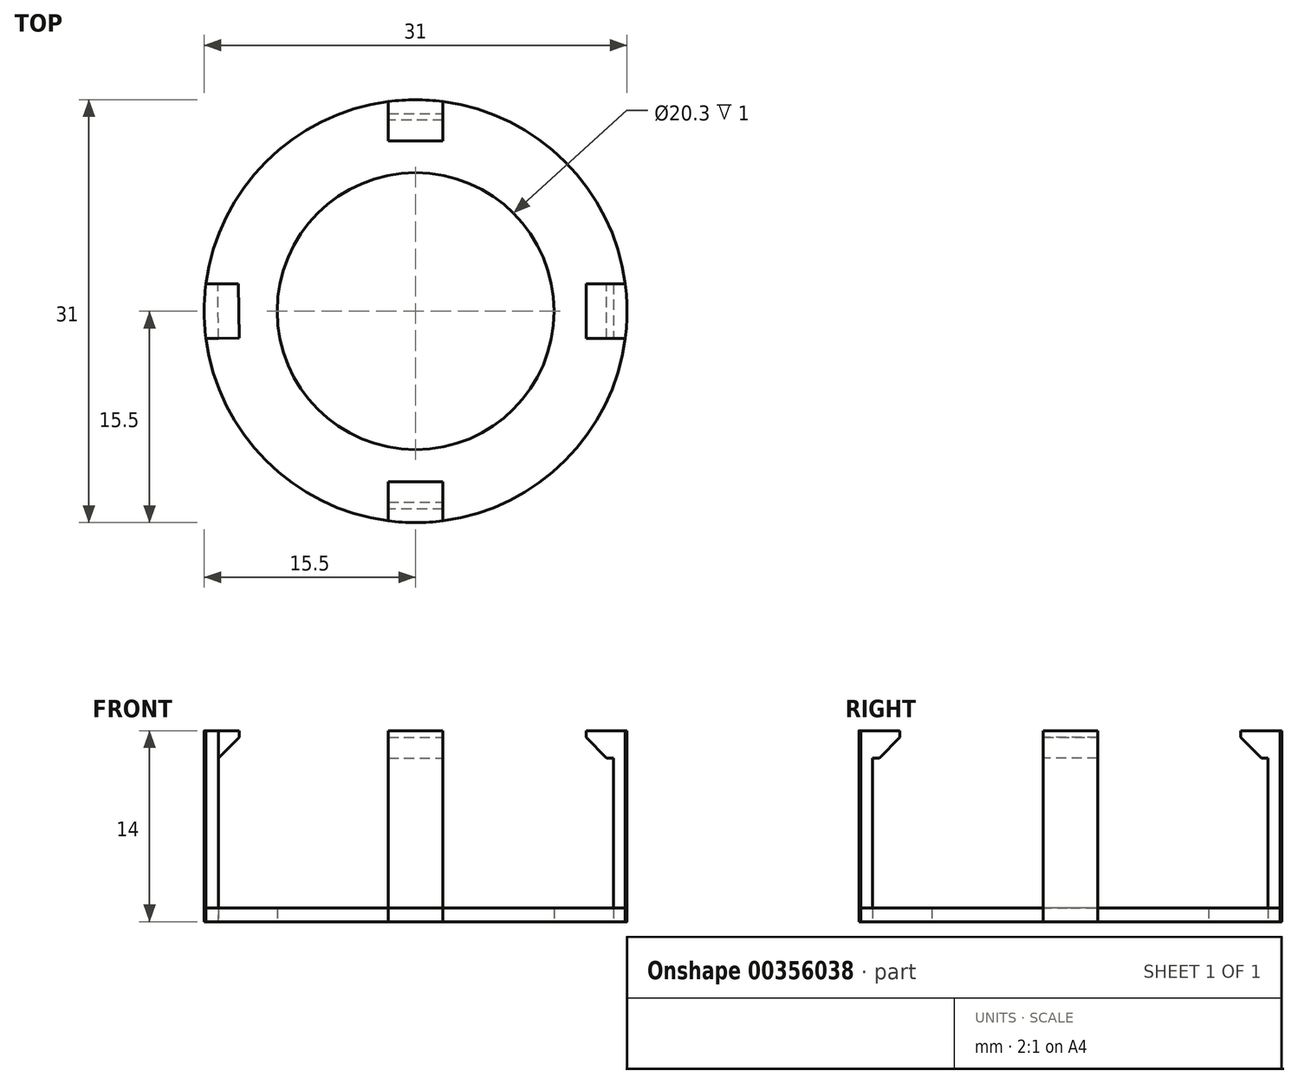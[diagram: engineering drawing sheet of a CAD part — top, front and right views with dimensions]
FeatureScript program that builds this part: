
annotation { "Feature Type Name" : "Feature", "Feature Type Description" : "" }
export const myFeature = defineFeature(function(context is Context, id is Id, definition is map)
    precondition{}
    {
        {
            var Q0;
            Q0=qCreatedBy(makeId("Top.planeOp"),FACE);
            var sketch = newSketch(context, id + "F0", { "sketchPlane" : qUnion([Q0])});
            skCircle(sketch, "E0", {"center": v(0, 0) * mm, "radius": 15.5 * mm});
            skCircle(sketch, "E1", {"center": v(0, 0) * mm, "radius": 10.15 * mm});
            skLineSegment(sketch, "E2.top", {"start": v(-2, 14.5) * mm, "end": v(2, 14.5) * mm});
            skLineSegment(sketch, "E2.left", {"start": v(-2, 15.37) * mm, "end": v(-2, 14.5) * mm});
            skLineSegment(sketch, "E2.right", {"start": v(2, 15.37) * mm, "end": v(2, 14.5) * mm});
            skPoint(sketch, "E2.middle", {"position": v(0, 14.93) * mm});
            skLineSegment(sketch, "E3.top", {"start": v(2, -14.5) * mm, "end": v(-2, -14.5) * mm});
            skLineSegment(sketch, "E3.left", {"start": v(2, -15.37) * mm, "end": v(2, -14.5) * mm});
            skLineSegment(sketch, "E3.right", {"start": v(-2, -15.37) * mm, "end": v(-2, -14.5) * mm});
            skPoint(sketch, "E3.middle", {"position": v(0, -14.93) * mm});
            skLineSegment(sketch, "E4.bottom", {"start": v(-15.37, -2) * mm, "end": v(-14.44, -2) * mm});
            skLineSegment(sketch, "E4.top", {"start": v(-15.43, 2) * mm, "end": v(-14.5, 2) * mm});
            skLineSegment(sketch, "E4.right", {"start": v(-14.44, -2) * mm, "end": v(-14.5, 2) * mm});
            skPoint(sketch, "E4.middle", {"position": v(-14.93, 0) * mm});
            skLineSegment(sketch, "E5.bottom", {"start": v(15.37, 2) * mm, "end": v(14.5, 2) * mm});
            skLineSegment(sketch, "E5.top", {"start": v(15.37, -2) * mm, "end": v(14.5, -2) * mm});
            skLineSegment(sketch, "E5.right", {"start": v(14.5, 2) * mm, "end": v(14.5, -2) * mm});
            skPoint(sketch, "E5.middle", {"position": v(14.93, 0) * mm});
            skSolve(sketch);
        }
        {
            var Q0;
            {var subQ0=sQuery(id+"F0.wireOp",EDGE,"E4.bottom");Q0=makeQuery(id+"F0.imprint","IMPRINT",FACE,{"disambiguationData":[TD([[makeQuery(id+"F0.imprint","IMPRINT",EDGE,{"derivedFrom":subQ0}),1.0]])]});}
            var Q1;
            Q1=makeQuery(id+"F0.imprint","IMPRINT",FACE,{"disambiguationData":[TD([[makeQuery(id+"F0.imprint","IMPRINT",EDGE,{"derivedFrom":sQuery(id+"F0.wireOp",EDGE,"E3.top")}),1.0]])]});
            var Q2;
            {var subQ0=sQuery(id+"F0.wireOp",EDGE,"TcTQrrII-gCTO-70l9-1had-G1OffKCwJlot.bottom");Q2=makeQuery(id+"F0.imprint","IMPRINT",FACE,{"disambiguationData":[TD([[makeQuery(id+"F0.imprint","IMPRINT",EDGE,{"derivedFrom":subQ0}),1.0]])]});}
            var Q3;
            Q3=makeQuery(id+"F0.imprint","IMPRINT",FACE,{"disambiguationData":[TD([[makeQuery(id+"F0.imprint","IMPRINT",EDGE,{"derivedFrom":sQuery(id+"F0.wireOp",EDGE,"E2.top")}),1.0]])]});
            var Q4;
            {var subQ0=sQuery(id+"F0.wireOp",EDGE,"VcLncp4H-A60G-CRBQ-irXQ-lvuzauZB2WbW.bottom");Q4=makeQuery(id+"F0.imprint","IMPRINT",FACE,{"disambiguationData":[TD([[makeQuery(id+"F0.imprint","IMPRINT",EDGE,{"derivedFrom":subQ0}),1.0]])]});}
            var Q5;
            {var subQ0=sQuery(id+"F0.wireOp",EDGE,"E5.bottom");Q5=makeQuery(id+"F0.imprint","IMPRINT",FACE,{"disambiguationData":[TD([[makeQuery(id+"F0.imprint","IMPRINT",EDGE,{"derivedFrom":subQ0}),1.0]])]});}
            extrude(context, id + "F1", {"entities" : qUnion([Q0, Q1, Q2, Q3, Q4, Q5]), "depth" : 14 * mm});
        }
        {
            var Q0;
            Q0=makeQuery(id+"F0.imprint","IMPRINT",FACE,{"disambiguationData":[TD([[makeQuery(id+"F0.imprint","IMPRINT",EDGE,{"derivedFrom":sQuery(id+"F0.wireOp",EDGE,"E2.top")}),1.0]])]});
            var Q1;
            {var subQ0=sQuery(id+"F0.wireOp",EDGE,"E4.bottom");Q1=makeQuery(id+"F0.imprint","IMPRINT",FACE,{"disambiguationData":[TD([[makeQuery(id+"F0.imprint","IMPRINT",EDGE,{"derivedFrom":subQ0}),1.0]])]});}
            var Q2;
            {var subQ0=sQuery(id+"F0.wireOp",EDGE,"TcTQrrII-gCTO-70l9-1had-G1OffKCwJlot.bottom");Q2=makeQuery(id+"F0.imprint","IMPRINT",FACE,{"disambiguationData":[TD([[makeQuery(id+"F0.imprint","IMPRINT",EDGE,{"derivedFrom":subQ0}),1.0]])]});}
            var Q3;
            Q3=makeQuery(id+"F0.imprint","IMPRINT",FACE,{"disambiguationData":[TD([[makeQuery(id+"F0.imprint","IMPRINT",EDGE,{"derivedFrom":sQuery(id+"F0.wireOp",EDGE,"E1")}),-1.0]])]});
            var Q4;
            Q4=makeQuery(id+"F0.imprint","IMPRINT",FACE,{"disambiguationData":[TD([[makeQuery(id+"F0.imprint","IMPRINT",EDGE,{"derivedFrom":sQuery(id+"F0.wireOp",EDGE,"E3.top")}),1.0]])]});
            extrude(context, id + "F2", {"entities" : qUnion([Q0, Q1, Q2, Q3, Q4]), "depth" : 1 * mm});
        }
        {
            var Q0;
            Q0=makeQuery(id+"F1.opExtrude","SWEPT_FACE",FACE,{"disambiguationData":[OSD([sQuery(id+"F0.wireOp",EDGE,"E3.top")])]});
            var sketch = newSketch(context, id + "F3", { "sketchPlane" : qUnion([Q0])});
            skLineSegment(sketch, "E6.bottom", {"start": v(-2, 14) * mm, "end": v(2, 14) * mm});
            skLineSegment(sketch, "E6.top", {"start": v(-2, 12) * mm, "end": v(2, 12) * mm});
            skLineSegment(sketch, "E6.left", {"start": v(-2, 14) * mm, "end": v(-2, 12) * mm});
            skLineSegment(sketch, "E6.right", {"start": v(2, 14) * mm, "end": v(2, 12) * mm});
            skSolve(sketch);
        }
        {
            var Q0;
            Q0=makeQuery(id+"F3.imprint","IMPRINT",FACE,{"disambiguationData":[TD([[makeQuery(id+"F3.imprint","IMPRINT",EDGE,{"derivedFrom":sQuery(id+"F3.wireOp",EDGE,"E6.bottom")}),-1.0]])]});
            extrude(context, id + "F4", {"entities" : qUnion([Q0]), "operationType" : NewBodyOperationType.ADD, "depth" : 2 * mm});
        }
        {
            var Q0;
            Q0=makeQuery(id+"F4.opExtrude","CAP_EDGE",EDGE,{"disambiguationData":[OSD([sQuery(id+"F3.wireOp",EDGE,"E6.top")])],"isStart":false});
            chamfer(context, id + "F5", {"entities" : qUnion([Q0]), "width" : 1.5 * mm, "tangentPropagation" : true});
        }
        {
            var Q0;
            Q0=makeQuery(id+"F1.opExtrude","SWEPT_FACE",FACE,{"disambiguationData":[OSD([sQuery(id+"F0.wireOp",EDGE,"E2.top")])]});
            var sketch = newSketch(context, id + "F6", { "sketchPlane" : qUnion([Q0])});
            skLineSegment(sketch, "E7.bottom", {"start": v(-2, 14) * mm, "end": v(2, 14) * mm});
            skLineSegment(sketch, "E7.top", {"start": v(-2, 12) * mm, "end": v(2, 12) * mm});
            skLineSegment(sketch, "E7.left", {"start": v(-2, 14) * mm, "end": v(-2, 12) * mm});
            skLineSegment(sketch, "E7.right", {"start": v(2, 14) * mm, "end": v(2, 12) * mm});
            skSolve(sketch);
        }
        {
            var Q0;
            Q0=makeQuery(id+"F6.imprint","IMPRINT",FACE,{"disambiguationData":[TD([[makeQuery(id+"F6.imprint","IMPRINT",EDGE,{"derivedFrom":sQuery(id+"F6.wireOp",EDGE,"E7.bottom")}),-1.0]])]});
            extrude(context, id + "F7", {"entities" : qUnion([Q0]), "operationType" : NewBodyOperationType.ADD, "depth" : 2 * mm});
        }
        {
            var Q0;
            Q0=makeQuery(id+"F7.opExtrude","CAP_EDGE",EDGE,{"disambiguationData":[OSD([sQuery(id+"F6.wireOp",EDGE,"E7.top")])],"isStart":false});
            chamfer(context, id + "F8", {"entities" : qUnion([Q0]), "width" : 1.5 * mm, "tangentPropagation" : true});
        }
        {
            var Q0;
            Q0=makeQuery(id+"F1.opExtrude","SWEPT_FACE",FACE,{"disambiguationData":[OSD([sQuery(id+"F0.wireOp",EDGE,"E4.right")])]});
            var sketch = newSketch(context, id + "F9", { "sketchPlane" : qUnion([Q0])});
            skLineSegment(sketch, "E8.bottom", {"start": v(-1.8, 14) * mm, "end": v(2.2, 14) * mm});
            skLineSegment(sketch, "E8.top", {"start": v(-1.8, 12) * mm, "end": v(2.2, 12) * mm});
            skLineSegment(sketch, "E8.left", {"start": v(-1.8, 14) * mm, "end": v(-1.8, 12) * mm});
            skLineSegment(sketch, "E8.right", {"start": v(2.2, 14) * mm, "end": v(2.2, 12) * mm});
            skSolve(sketch);
        }
        {
            var Q0;
            Q0=makeQuery(id+"F9.imprint","IMPRINT",FACE,{"disambiguationData":[TD([[makeQuery(id+"F9.imprint","IMPRINT",EDGE,{"derivedFrom":sQuery(id+"F9.wireOp",EDGE,"E8.bottom")}),-1.0]])]});
            extrude(context, id + "F10", {"entities" : qUnion([Q0]), "operationType" : NewBodyOperationType.ADD, "depth" : 1.5 * mm});
        }
        {
            var Q0;
            Q0=makeQuery(id+"F10.opExtrude","CAP_EDGE",EDGE,{"disambiguationData":[OSD([sQuery(id+"F9.wireOp",EDGE,"E8.top")])],"isStart":false});
            chamfer(context, id + "F11", {"entities" : qUnion([Q0]), "width" : 1.5 * mm, "tangentPropagation" : true});
        }
        {
            var Q0;
            Q0=makeQuery(id+"F1.opExtrude","SWEPT_FACE",FACE,{"disambiguationData":[OSD([sQuery(id+"F0.wireOp",EDGE,"E5.right")])]});
            var sketch = newSketch(context, id + "F12", { "sketchPlane" : qUnion([Q0])});
            skLineSegment(sketch, "E9.bottom", {"start": v(-2, 14) * mm, "end": v(2, 14) * mm});
            skLineSegment(sketch, "E9.top", {"start": v(-2, 12) * mm, "end": v(2, 12) * mm});
            skLineSegment(sketch, "E9.left", {"start": v(-2, 14) * mm, "end": v(-2, 12) * mm});
            skLineSegment(sketch, "E9.right", {"start": v(2, 14) * mm, "end": v(2, 12) * mm});
            skSolve(sketch);
        }
        {
            var Q0;
            Q0=makeQuery(id+"F12.imprint","IMPRINT",FACE,{"disambiguationData":[TD([[makeQuery(id+"F12.imprint","IMPRINT",EDGE,{"derivedFrom":sQuery(id+"F12.wireOp",EDGE,"E9.bottom")}),-1.0]])]});
            extrude(context, id + "F13", {"entities" : qUnion([Q0]), "operationType" : NewBodyOperationType.ADD, "depth" : 2 * mm});
        }
        {
            var Q0;
            Q0=makeQuery(id+"F13.opExtrude","CAP_EDGE",EDGE,{"disambiguationData":[OSD([sQuery(id+"F12.wireOp",EDGE,"E9.top")])],"isStart":false});
            chamfer(context, id + "F14", {"entities" : qUnion([Q0]), "width" : 1.5 * mm, "tangentPropagation" : true});
        }
    });
